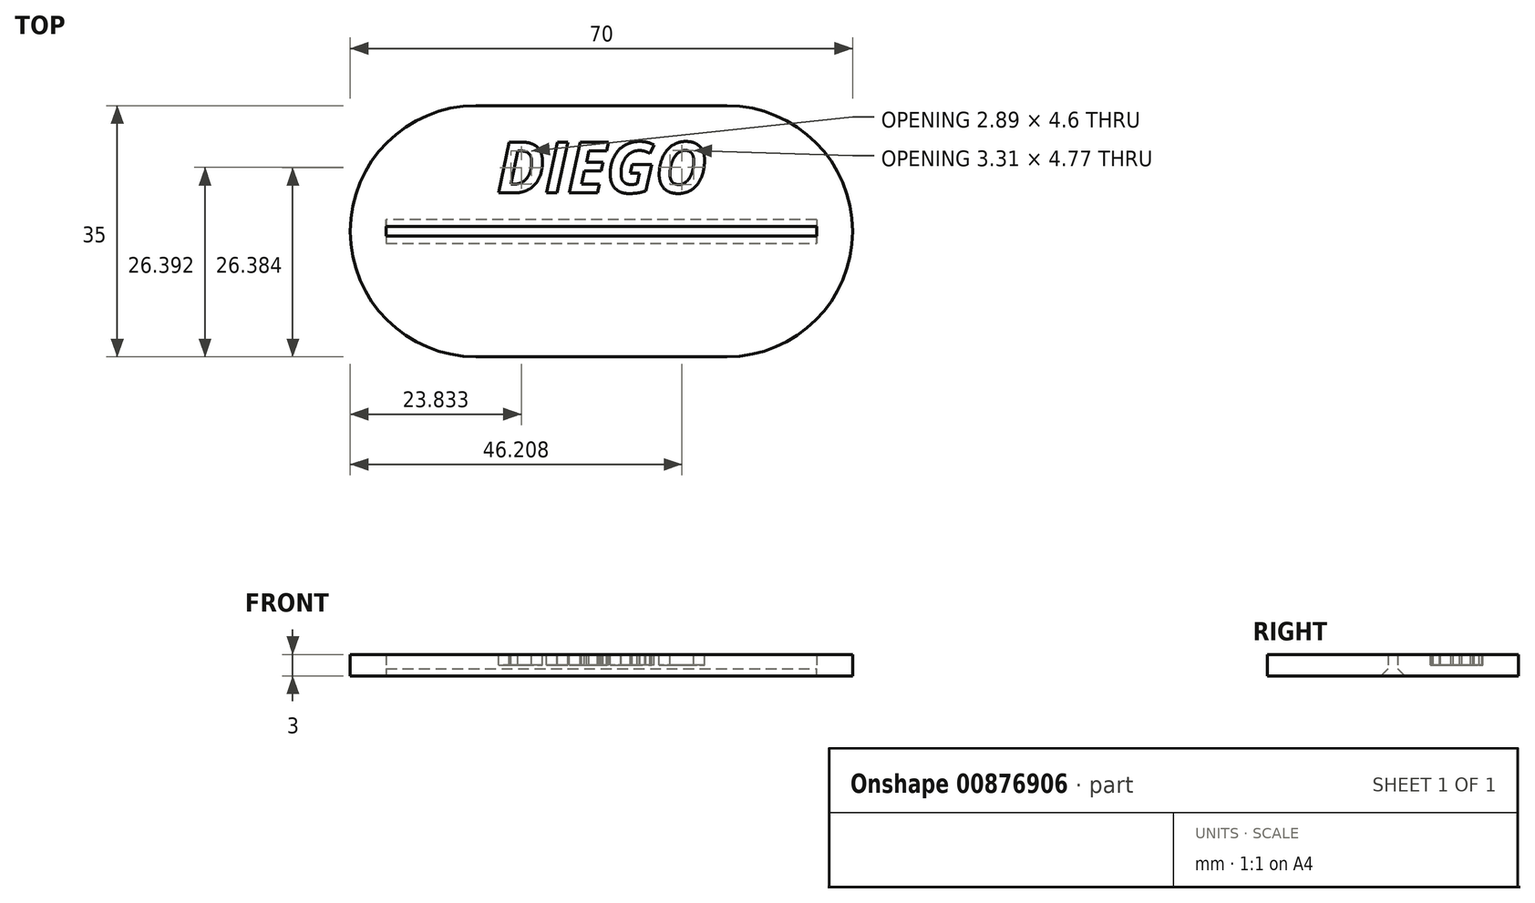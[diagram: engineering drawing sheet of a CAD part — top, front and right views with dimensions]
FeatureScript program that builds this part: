
annotation { "Feature Type Name" : "Feature", "Feature Type Description" : "" }
export const myFeature = defineFeature(function(context is Context, id is Id, definition is map)
    precondition{}
    {
        {
            var Q0;
            Q0=qCreatedBy(makeId("Top.planeOp"),FACE);
            var sketch = newSketch(context, id + "F0", { "sketchPlane" : qUnion([Q0])});
            skLineSegment(sketch, "E0.bottom", {"start": v(0, 0) * mm, "end": v(70, 0) * mm});
            skLineSegment(sketch, "E0.top", {"start": v(0, 35) * mm, "end": v(70, 35) * mm});
            skLineSegment(sketch, "E0.left", {"start": v(0, 0) * mm, "end": v(0, 35) * mm});
            skLineSegment(sketch, "E0.right", {"start": v(70, 0) * mm, "end": v(70, 35) * mm});
            skLineSegment(sketch, "E1.bottom", {"start": v(5, 18.15) * mm, "end": v(65, 18.15) * mm});
            skLineSegment(sketch, "E1.top", {"start": v(5, 16.85) * mm, "end": v(65, 16.85) * mm});
            skLineSegment(sketch, "E1.left", {"start": v(5, 18.15) * mm, "end": v(5, 16.85) * mm});
            skLineSegment(sketch, "E1.right", {"start": v(65, 18.15) * mm, "end": v(65, 16.85) * mm});
            skSolve(sketch);
        }
        {
            var Q0;
            Q0=qSketchRegion(id+"F0",true);
            extrude(context, id + "F1", {"entities" : qUnion([Q0]), "depth" : 3 * mm, "offsetDistance" : 25 * mm});
        }
        {
            var Q0;
            Q0=makeQuery(id+"F1.opExtrude","SWEPT_EDGE",EDGE,{"disambiguationData":[OSD([sQuery(id+"F0.wireOp",EDGE,"E0.bottom"),sQuery(id+"F0.wireOp",EDGE,"E0.right")])]});
            var Q1;
            Q1=makeQuery(id+"F1.opExtrude","SWEPT_EDGE",EDGE,{"disambiguationData":[OSD([sQuery(id+"F0.wireOp",EDGE,"E0.top"),sQuery(id+"F0.wireOp",EDGE,"E0.right")])]});
            var Q2;
            Q2=makeQuery(id+"F1.opExtrude","SWEPT_EDGE",EDGE,{"disambiguationData":[OSD([sQuery(id+"F0.wireOp",EDGE,"E0.top"),sQuery(id+"F0.wireOp",EDGE,"E0.left")])]});
            var Q3;
            Q3=makeQuery(id+"F1.opExtrude","SWEPT_EDGE",EDGE,{"disambiguationData":[OSD([sQuery(id+"F0.wireOp",EDGE,"E0.bottom"),sQuery(id+"F0.wireOp",EDGE,"E0.left")])]});
            fillet(context, id + "F2", {"entities" : qUnion([Q0, Q1, Q2, Q3]), "radius" : 17.5 * mm, "tangentPropagation" : true, "allowEdgeOverflow" : false});
        }
        {
            var Q0;
            Q0=makeQuery(id+"F1.opExtrude","CAP_EDGE",EDGE,{"disambiguationData":[OSD([sQuery(id+"F0.wireOp",EDGE,"E1.top")])],"isStart":true});
            var Q1;
            Q1=makeQuery(id+"F1.opExtrude","CAP_EDGE",EDGE,{"disambiguationData":[OSD([sQuery(id+"F0.wireOp",EDGE,"E1.bottom")])],"isStart":true});
            chamfer(context, id + "F3", {"entities" : qUnion([Q0, Q1]), "width" : 1 * mm, "tangentPropagation" : true});
        }
        {
            var Q0;
            Q0=makeQuery(id+"F1.opExtrude","CAP_FACE",FACE,{"disambiguationData":[OSD([sQuery(id+"F0.wireOp",EDGE,"E0.bottom"),sQuery(id+"F0.wireOp",EDGE,"E0.top"),sQuery(id+"F0.wireOp",EDGE,"E0.left"),sQuery(id+"F0.wireOp",EDGE,"E0.right"),sQuery(id+"F0.wireOp",EDGE,"E1.bottom"),sQuery(id+"F0.wireOp",EDGE,"E1.top"),sQuery(id+"F0.wireOp",EDGE,"E1.left"),sQuery(id+"F0.wireOp",EDGE,"E1.right")])],"isStart":false});
            var sketch = newSketch(context, id + "F4", { "sketchPlane" : qUnion([Q0])});
            skText(sketch, "E2", { "text": "DIEGO", "fontName": "OpenSans-BoldItalic.ttf"});
            const initialGuessF4  = {"E2": [0.0204, 0.02285, 1, 0, 0.00712]};
            skSetInitialGuess(sketch, initialGuessF4);
            skSolve(sketch);
        }
        {
            var Q0;
            Q0 = qSketchRegion(id + "F4", true);
            extrude(context, id + "F5", {"entities" : qUnion([Q0]), "oppositeDirection" : true, "depth" : 1.5 * mm, "offsetDistance" : 25 * mm});
        }
    });
